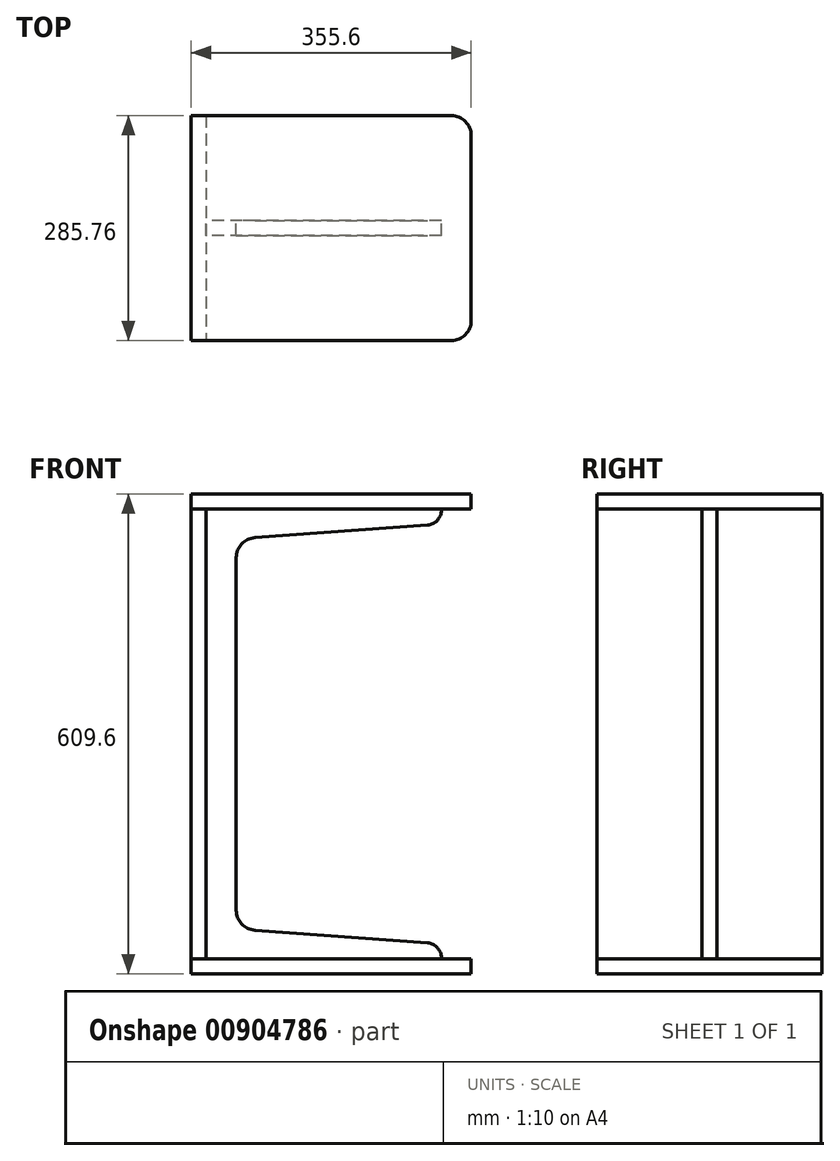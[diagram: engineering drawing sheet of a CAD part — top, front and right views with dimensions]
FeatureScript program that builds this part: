
annotation { "Feature Type Name" : "Feature", "Feature Type Description" : "" }
export const myFeature = defineFeature(function(context is Context, id is Id, definition is map)
    precondition{}
    {
        {
            var Q0;
            Q0=qCreatedBy(makeId("Front.planeOp"),FACE);
            var sketch = newSketch(context, id + "F0", { "sketchPlane" : qUnion([Q0])});
            skLineSegment(sketch, "E0", {"start": v(355.6, 0) * mm, "end": v(0, 0) * mm});
            skLineSegment(sketch, "E1", {"start": v(0, 0) * mm, "end": v(0, 609.6) * mm});
            skLineSegment(sketch, "E2", {"start": v(0, 609.6) * mm, "end": v(355.6, 609.6) * mm});
            skLineSegment(sketch, "E3", {"start": v(355.6, 609.6) * mm, "end": v(355.6, 590.55) * mm});
            skLineSegment(sketch, "E4", {"start": v(355.6, 590.55) * mm, "end": v(19.05, 590.55) * mm});
            skLineSegment(sketch, "E5", {"start": v(19.05, 590.55) * mm, "end": v(19.05, 19.05) * mm});
            skLineSegment(sketch, "E6", {"start": v(19.05, 19.05) * mm, "end": v(355.6, 19.05) * mm});
            skLineSegment(sketch, "E7", {"start": v(355.6, 19.05) * mm, "end": v(355.6, 0) * mm});
            skLineSegment(sketch, "E8", {"start": v(19.05, 590.55) * mm, "end": v(0, 590.55) * mm});
            skLineSegment(sketch, "E9", {"start": v(19.05, 19.05) * mm, "end": v(0, 19.05) * mm});
            skLineSegment(sketch, "E10", {"start": v(317.67, 590.55) * mm, "end": v(317.67, 571.5) * mm});
            skLineSegment(sketch, "E11", {"start": v(57.15, 552.45) * mm, "end": v(57.15, 57.15) * mm});
            skLineSegment(sketch, "E12", {"start": v(317.67, 38.1) * mm, "end": v(317.67, 19.05) * mm});
            skLineSegment(sketch, "E13", {"start": v(57.15, 552.45) * mm, "end": v(19.05, 552.45) * mm, "construction": true});
            skLineSegment(sketch, "E14", {"start": v(57.15, 552.45) * mm, "end": v(317.67, 571.5) * mm});
            skLineSegment(sketch, "E15", {"start": v(57.15, 57.15) * mm, "end": v(317.67, 38.1) * mm});
            skLineSegment(sketch, "E16", {"start": v(0, 304.8) * mm, "end": v(553.49, 304.8) * mm, "construction": true});
            skLineSegment(sketch, "E17", {"start": v(57.15, 552.45) * mm, "end": v(57.15, 590.55) * mm, "construction": true});
            skSolve(sketch);
        }
        {
            var Q0;
            {var subQ3=sQuery(id+"F0.wireOp",EDGE,"E2");Q0=makeQuery(id+"F0.imprint","IMPRINT",FACE,{"disambiguationData":[TD([[makeQuery(id+"F0.imprint","IMPRINT",EDGE,{"derivedFrom":subQ3}),-1.0]])]});}
            extrude(context, id + "F1", {"entities" : qUnion([Q0]), "endBound" : BoundingType.SYMMETRIC, "oppositeDirection" : true, "depth" : 285.75 * mm, "offsetDistance" : 25.4 * mm});
        }
        {
            var Q0;
            Q0=makeQuery(id+"F0.imprint","IMPRINT",FACE,{"disambiguationData":[TD([[makeQuery(id+"F0.imprint","IMPRINT",EDGE,{"derivedFrom":sQuery(id+"F0.wireOp",EDGE,"E5")}),-1.0]])]});
            var Q1;
            Q1=makeQuery(id+"F1.opExtrude","CAP_FACE",FACE,{"disambiguationData":[OSD([sQuery(id+"F0.wireOp",EDGE,"E1"),sQuery(id+"F0.wireOp",EDGE,"E2"),sQuery(id+"F0.wireOp",EDGE,"E3"),sQuery(id+"F0.wireOp",EDGE,"E4"),sQuery(id+"F0.wireOp",EDGE,"E8")])],"isStart":false});
            var Q2;
            Q2=makeQuery(id+"F1.opExtrude","CAP_FACE",FACE,{"disambiguationData":[OSD([sQuery(id+"F0.wireOp",EDGE,"E1"),sQuery(id+"F0.wireOp",EDGE,"E2"),sQuery(id+"F0.wireOp",EDGE,"E3"),sQuery(id+"F0.wireOp",EDGE,"E4"),sQuery(id+"F0.wireOp",EDGE,"E8")])],"isStart":true});
            extrude(context, id + "F2", {"entities" : qUnion([Q0]), "endBound" : BoundingType.UP_TO_SURFACE, "oppositeDirection" : true, "depth" : 25.4 * mm, "endBoundEntityFace" : qUnion([Q1]), "offsetDistance" : 25.4 * mm, "hasSecondDirection" : true, "secondDirectionBound" : SecondDirectionBoundingType.UP_TO_SURFACE, "secondDirectionOppositeDirection" : false, "secondDirectionDepth" : 25.4 * mm, "secondDirectionBoundEntityFace" : qUnion([Q2])});
        }
        {
            var Q0;
            {var subQ4=sQuery(id+"F0.wireOp",EDGE,"E0");Q0=makeQuery(id+"F0.imprint","IMPRINT",FACE,{"disambiguationData":[TD([[makeQuery(id+"F0.imprint","IMPRINT",EDGE,{"derivedFrom":subQ4}),-1.0]])]});}
            var Q1;
            Q1=makeQuery(id+"F2.opExtrude","CAP_FACE",FACE,{"disambiguationData":[OSD([sQuery(id+"F0.wireOp",EDGE,"E1"),sQuery(id+"F0.wireOp",EDGE,"E5"),sQuery(id+"F0.wireOp",EDGE,"E8"),sQuery(id+"F0.wireOp",EDGE,"E9")])],"isStart":true});
            var Q2;
            Q2=makeQuery(id+"F2.opExtrude","CAP_FACE",FACE,{"disambiguationData":[OSD([sQuery(id+"F0.wireOp",EDGE,"E1"),sQuery(id+"F0.wireOp",EDGE,"E5"),sQuery(id+"F0.wireOp",EDGE,"E8"),sQuery(id+"F0.wireOp",EDGE,"E9")])],"isStart":false});
            extrude(context, id + "F3", {"entities" : qUnion([Q0]), "endBound" : BoundingType.UP_TO_SURFACE, "depth" : 25.4 * mm, "endBoundEntityFace" : qUnion([Q1]), "offsetDistance" : 25.4 * mm, "hasSecondDirection" : true, "secondDirectionBound" : SecondDirectionBoundingType.UP_TO_SURFACE, "secondDirectionOppositeDirection" : true, "secondDirectionDepth" : 25.4 * mm, "secondDirectionBoundEntityFace" : qUnion([Q2])});
        }
        {
            var Q0;
            {var subQ2=sQuery(id+"F0.wireOp",EDGE,"E5");Q0=makeQuery(id+"F0.imprint","IMPRINT",FACE,{"disambiguationData":[TD([[makeQuery(id+"F0.imprint","IMPRINT",EDGE,{"derivedFrom":subQ2}),1.0]])]});}
            extrude(context, id + "F4", {"entities" : qUnion([Q0]), "endBound" : BoundingType.SYMMETRIC, "depth" : 19.05 * mm, "offsetDistance" : 25.4 * mm});
        }
        {
            var Q0;
            Q0=makeQuery(id+"F4.opExtrude","SWEPT_EDGE",EDGE,{"disambiguationData":[OSD([sQuery(id+"F0.wireOp",EDGE,"E11"),sQuery(id+"F0.wireOp",EDGE,"E14")])]});
            var Q1;
            Q1=makeQuery(id+"F4.opExtrude","SWEPT_EDGE",EDGE,{"disambiguationData":[OSD([sQuery(id+"F0.wireOp",EDGE,"E11"),sQuery(id+"F0.wireOp",EDGE,"E15")])]});
            fillet(context, id + "F5", {"entities" : qUnion([Q0, Q1]), "radius" : 25.4 * mm, "tangentPropagation" : true, "allowEdgeOverflow" : false});
        }
        {
            var Q0;
            Q0=makeQuery(id+"F4.opExtrude","SWEPT_EDGE",EDGE,{"disambiguationData":[OSD([sQuery(id+"F0.wireOp",EDGE,"E10"),sQuery(id+"F0.wireOp",EDGE,"E14")])]});
            var Q1;
            Q1=makeQuery(id+"F4.opExtrude","SWEPT_EDGE",EDGE,{"disambiguationData":[OSD([sQuery(id+"F0.wireOp",EDGE,"E12"),sQuery(id+"F0.wireOp",EDGE,"E15")])]});
            fillet(context, id + "F6", {"entities" : qUnion([Q0, Q1]), "radius" : 19.05 * mm, "tangentPropagation" : true, "allowEdgeOverflow" : false});
        }
        {
            var Q0;
            Q0=makeQuery(id+"F1.opExtrude","CAP_EDGE",EDGE,{"disambiguationData":[OSD([sQuery(id+"F0.wireOp",EDGE,"E3")])],"isStart":true});
            var Q1;
            Q1=makeQuery(id+"F1.opExtrude","CAP_EDGE",EDGE,{"disambiguationData":[OSD([sQuery(id+"F0.wireOp",EDGE,"E3")])],"isStart":false});
            var Q2;
            Q2=makeQuery(id+"F3.opExtrude","CAP_EDGE",EDGE,{"disambiguationData":[OSD([sQuery(id+"F0.wireOp",EDGE,"E7")])],"isStart":true});
            var Q3;
            Q3=makeQuery(id+"F3.opExtrude","CAP_EDGE",EDGE,{"disambiguationData":[OSD([sQuery(id+"F0.wireOp",EDGE,"E7")])],"isStart":false});
            fillet(context, id + "F7", {"entities" : qUnion([Q0, Q1, Q2, Q3]), "radius" : 25.4 * mm, "tangentPropagation" : true, "allowEdgeOverflow" : false});
        }
    });
